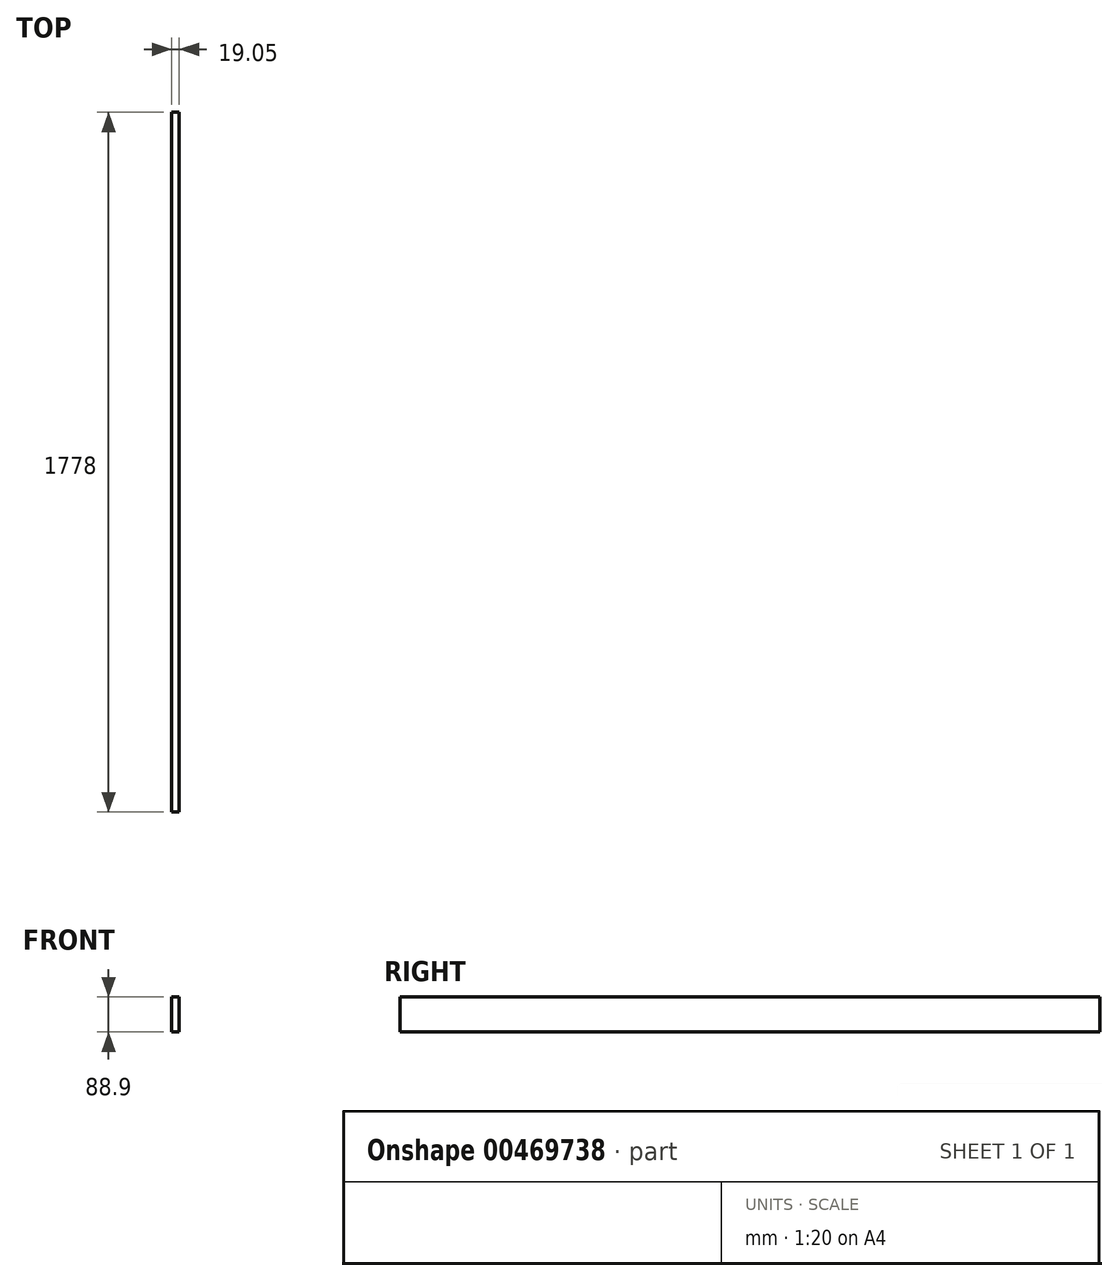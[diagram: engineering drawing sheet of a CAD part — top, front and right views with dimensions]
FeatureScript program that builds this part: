
annotation { "Feature Type Name" : "Feature", "Feature Type Description" : "" }
export const myFeature = defineFeature(function(context is Context, id is Id, definition is map)
    precondition{}
    {
        {
            var Q0;
            Q0=qCreatedBy(makeId("Right.planeOp"),FACE);
            var sketch = newSketch(context, id + "F0", { "sketchPlane" : qUnion([Q0])});
            skLineSegment(sketch, "E0.bottom", {"start": v(0, 0) * mm, "end": v(1778, 0) * mm});
            skLineSegment(sketch, "E0.top", {"start": v(0, 88.9) * mm, "end": v(1778, 88.9) * mm});
            skLineSegment(sketch, "E0.left", {"start": v(0, 0) * mm, "end": v(0, 88.9) * mm});
            skLineSegment(sketch, "E0.right", {"start": v(1778, 0) * mm, "end": v(1778, 88.9) * mm});
            skSolve(sketch);
        }
        {
            var Q0;
            Q0=makeQuery(id+"F0.imprint","IMPRINT",FACE,{"disambiguationData":[TD([[makeQuery(id+"F0.imprint","IMPRINT",EDGE,{"derivedFrom":sQuery(id+"F0.wireOp",EDGE,"E0.bottom")}),1.0]])]});
            extrude(context, id + "F1", {"entities" : qUnion([Q0]), "depth" : 19.05 * mm, "offsetDistance" : 25.4 * mm});
        }
    });
